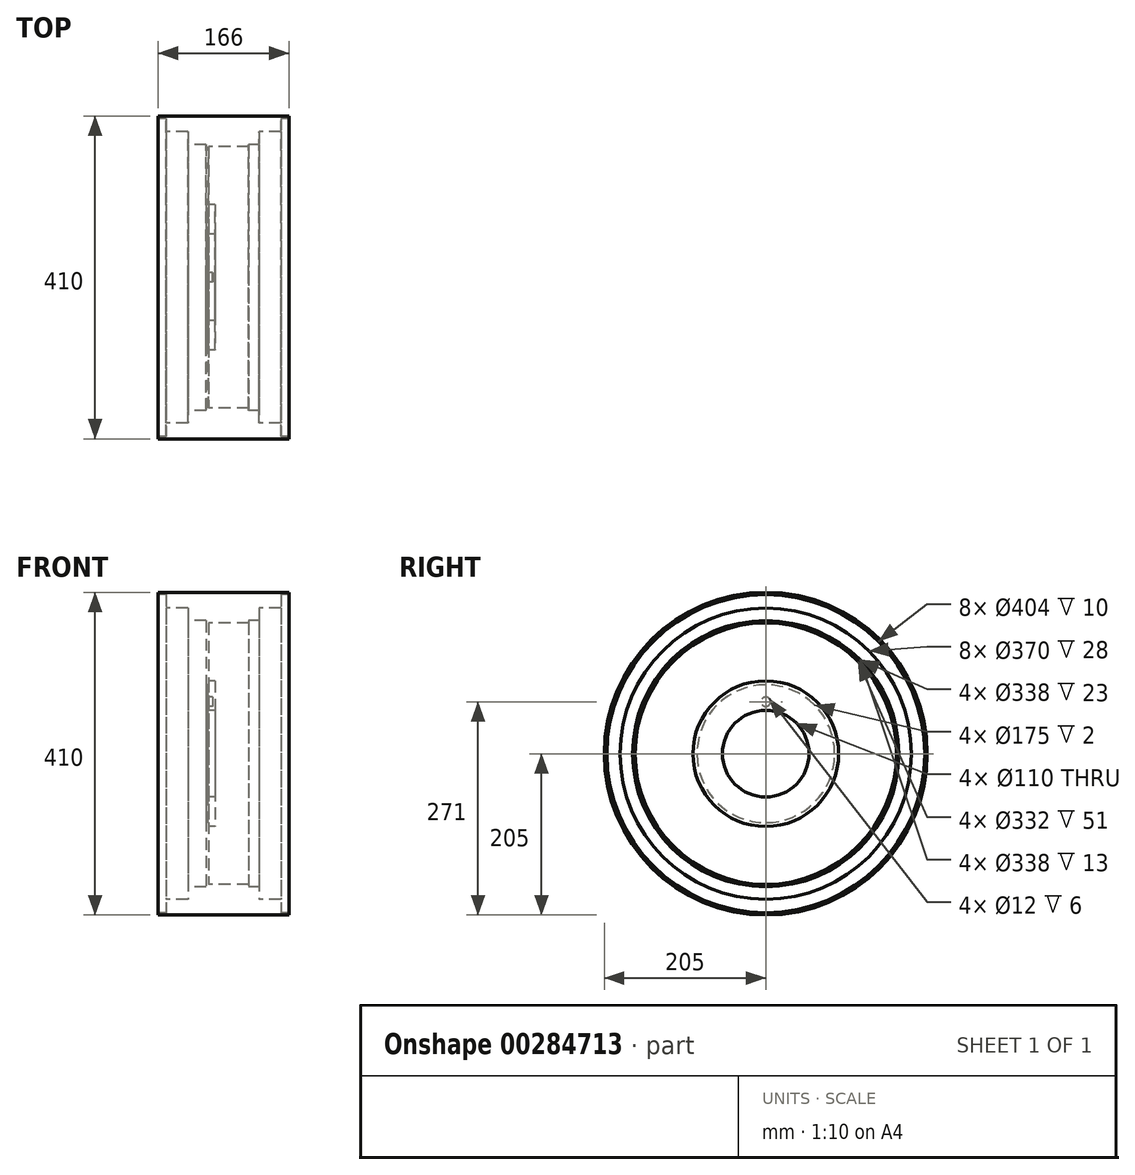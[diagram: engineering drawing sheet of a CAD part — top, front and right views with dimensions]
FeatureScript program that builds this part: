
annotation { "Feature Type Name" : "Feature", "Feature Type Description" : "" }
export const myFeature = defineFeature(function(context is Context, id is Id, definition is map)
    precondition{}
    {
        {
            var Q0;
            Q0=qCreatedBy(makeId("Front.planeOp"),FACE);
            var sketch = newSketch(context, id + "F0", { "sketchPlane" : qUnion([Q0])});
            skLineSegment(sketch, "E0", {"start": v(0, 0) * mm, "end": v(0, 205) * mm, "construction": true});
            skLineSegment(sketch, "E1", {"start": v(0, 205) * mm, "end": v(166, 205) * mm});
            skLineSegment(sketch, "E2", {"start": v(166, 205) * mm, "end": v(166, 202) * mm});
            skLineSegment(sketch, "E3", {"start": v(166, 202) * mm, "end": v(156, 202) * mm});
            skLineSegment(sketch, "E4", {"start": v(0, 0) * mm, "end": v(166, 0) * mm, "construction": true});
            skLineSegment(sketch, "E5", {"start": v(156, 0) * mm, "end": v(156, 185) * mm, "construction": true});
            skLineSegment(sketch, "E6", {"start": v(156, 202) * mm, "end": v(156, 185) * mm});
            skLineSegment(sketch, "E7", {"start": v(156, 185) * mm, "end": v(128, 185) * mm});
            skLineSegment(sketch, "E8", {"start": v(128, 0) * mm, "end": v(128, 169) * mm, "construction": true});
            skLineSegment(sketch, "E9", {"start": v(128, 185) * mm, "end": v(128, 169) * mm});
            skLineSegment(sketch, "E10", {"start": v(128, 169) * mm, "end": v(115, 169) * mm});
            skLineSegment(sketch, "E11", {"start": v(115, 169) * mm, "end": v(115, 166) * mm});
            skLineSegment(sketch, "E12", {"start": v(115, 166) * mm, "end": v(64, 166) * mm});
            skLineSegment(sketch, "E13", {"start": v(0, 205) * mm, "end": v(0, 202) * mm});
            skLineSegment(sketch, "E14", {"start": v(0, 202) * mm, "end": v(10, 202) * mm});
            skLineSegment(sketch, "E15", {"start": v(10, 202) * mm, "end": v(10, 185) * mm});
            skLineSegment(sketch, "E16", {"start": v(10, 185) * mm, "end": v(38, 185) * mm});
            skLineSegment(sketch, "E17", {"start": v(38, 185) * mm, "end": v(38, 169) * mm});
            skLineSegment(sketch, "E18", {"start": v(38, 169) * mm, "end": v(61, 169) * mm});
            skPoint(sketch, "E19", {"position": v(72, 205) * mm});
            skLineSegment(sketch, "E20", {"start": v(72, 205) * mm, "end": v(72, 0) * mm, "construction": true});
            skPoint(sketch, "E21", {"position": v(72, 92.5) * mm});
            skPoint(sketch, "E22", {"position": v(282.36, 5.68) * mm});
            skLineSegment(sketch, "E23", {"start": v(64, 166) * mm, "end": v(64, 92.5) * mm});
            skLineSegment(sketch, "E24", {"start": v(64, 92.5) * mm, "end": v(72, 92.5) * mm});
            skPoint(sketch, "E25", {"position": v(72, 55) * mm});
            skLineSegment(sketch, "E26", {"start": v(72, 92.5) * mm, "end": v(72, 55) * mm});
            skPoint(sketch, "E27", {"position": v(72, 87.5) * mm});
            skLineSegment(sketch, "E28", {"start": v(61, 169) * mm, "end": v(61, 87.5) * mm});
            skLineSegment(sketch, "E29", {"start": v(61, 87.5) * mm, "end": v(63, 87.5) * mm});
            skLineSegment(sketch, "E30", {"start": v(63, 87.5) * mm, "end": v(63, 55) * mm});
            skLineSegment(sketch, "E31", {"start": v(63, 55) * mm, "end": v(72, 55) * mm});
            skSolve(sketch);
        }
        {
            var Q0;
            Q0=qSketchRegion(id+"F0",true);
            var Q1;
            Q1=sQuery(id+"F0.wireOp",EDGE,"E4");
            revolve(context, id + "F1", {"entities" : qUnion([Q0]), "axis" : qUnion([Q1]), "revolveType" : RevolveType.FULL});
        }
        {
            var Q0;
            Q0=makeQuery(id+"F1.opRevolve","SWEPT_FACE",FACE,{"disambiguationData":[OSD([sQuery(id+"F0.wireOp",EDGE,"E30")])]});
            var sketch = newSketch(context, id + "F2", { "sketchPlane" : qUnion([Q0])});
            skPoint(sketch, "E32", {"position": v(0, 66) * mm});
            skCircle(sketch, "E33", {"center": v(0, 66) * mm, "radius": 6 * mm});
            skSolve(sketch);
        }
        {
            var Q0;
            Q0=qSketchRegion(id+"F2",true);
            extrude(context, id + "F3", {"entities" : qUnion([Q0]), "operationType" : NewBodyOperationType.REMOVE, "oppositeDirection" : true, "depth" : 6 * mm});
        }
    });
